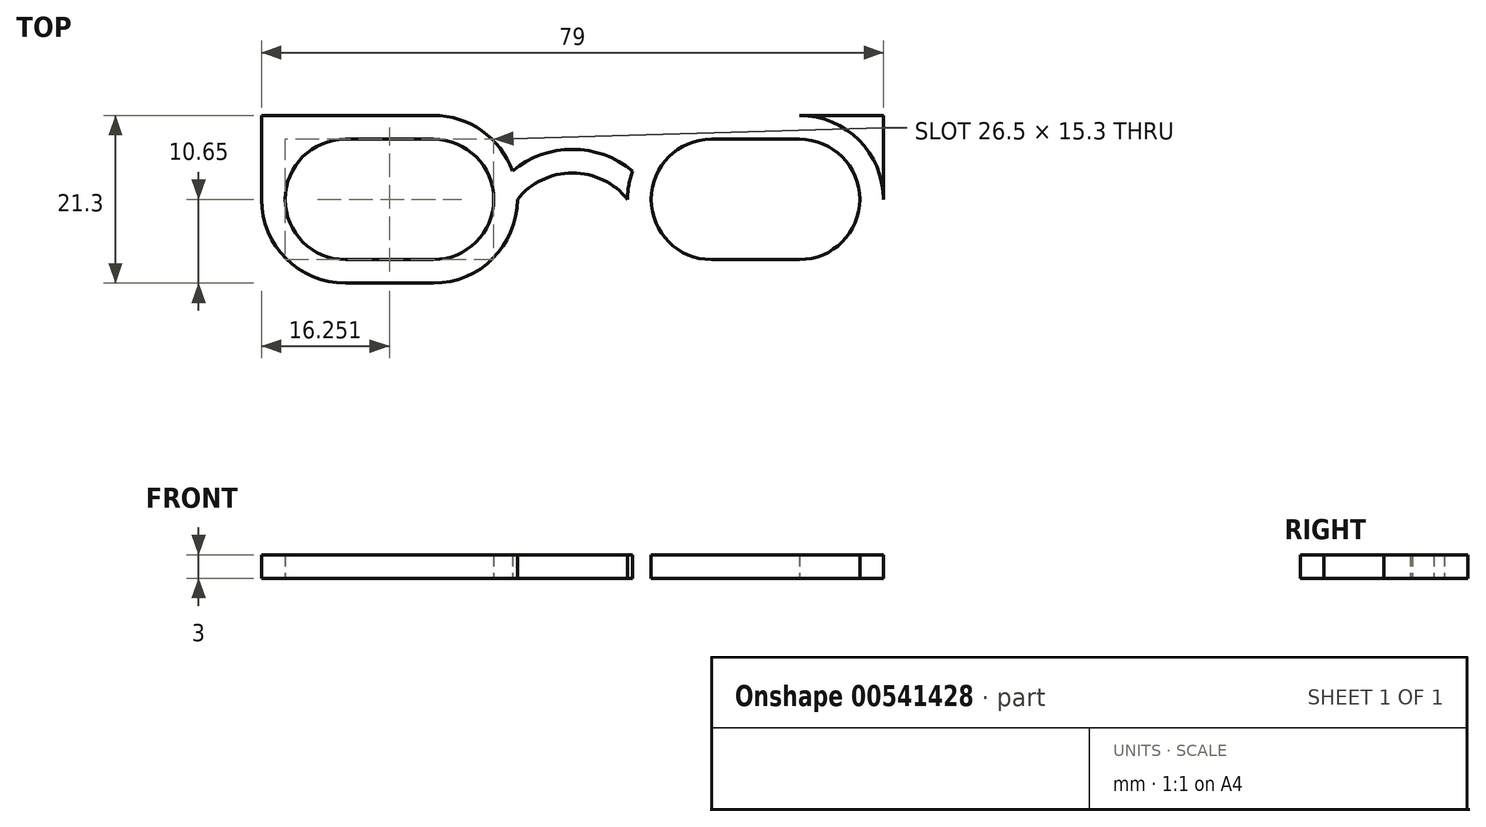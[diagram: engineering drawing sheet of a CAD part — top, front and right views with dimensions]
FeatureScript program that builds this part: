
annotation { "Feature Type Name" : "Feature", "Feature Type Description" : "" }
export const myFeature = defineFeature(function(context is Context, id is Id, definition is map)
    precondition{}
    {
        {
            var Q0;
            Q0=qCreatedBy(makeId("Top.planeOp"),FACE);
            var sketch = newSketch(context, id + "F0", { "sketchPlane" : qUnion([Q0])});
            skLineSegment(sketch, "E0", {"start": v(0, 24.47) * mm, "end": v(0, -25.63) * mm, "construction": true});
            skPoint(sketch, "E1", {"position": v(0, -41.55) * mm});
            skLineSegment(sketch, "E2", {"start": v(-35, -41.55) * mm, "end": v(35, -41.55) * mm, "construction": true});
            skPoint(sketch, "E3", {"position": v(-10, 0) * mm});
            skArc(sketch, "E4", {"start": v(-17.65, -7.65) * mm, "mid": v(-10, 0) * mm, "end": v(-17.65, 7.65) * mm});
            skLineSegment(sketch, "E5", {"start": v(-17.65, -7.65) * mm, "end": v(-28.85, -7.65) * mm});
            skLineSegment(sketch, "E6", {"start": v(-17.65, 7.65) * mm, "end": v(-28.85, 7.65) * mm});
            skArc(sketch, "E7", {"start": v(-28.85, 7.65) * mm, "mid": v(-36.5, 0) * mm, "end": v(-28.85, -7.65) * mm});
            skArc(sketch, "E8.MirrorCS", {"start": v(17.65, -7.65) * mm, "mid": v(10, 0) * mm, "end": v(17.65, 7.65) * mm});
            skLineSegment(sketch, "E9.MirrorCS", {"start": v(17.65, 7.65) * mm, "end": v(28.85, 7.65) * mm});
            skLineSegment(sketch, "E10.MirrorCS", {"start": v(17.65, -7.65) * mm, "end": v(28.85, -7.65) * mm});
            skArc(sketch, "E11.MirrorCS", {"start": v(28.85, 7.65) * mm, "mid": v(36.5, 0) * mm, "end": v(28.85, -7.65) * mm});
            skPoint(sketch, "E12", {"position": v(10, 0) * mm});
            skArc(sketch, "E13.0", {"start": v(-28.85, 10.65) * mm, "mid": v(-39.5, 0) * mm, "end": v(-28.85, -10.65) * mm});
            skLineSegment(sketch, "E13.1", {"start": v(-17.65, 10.65) * mm, "end": v(-28.85, 10.65) * mm});
            skArc(sketch, "E13.2", {"start": v(-17.65, -10.65) * mm, "mid": v(-7, 0) * mm, "end": v(-17.65, 10.65) * mm});
            skLineSegment(sketch, "E13.3", {"start": v(-17.65, -10.65) * mm, "end": v(-28.85, -10.65) * mm});
            skArc(sketch, "E14.MirrorCS", {"start": v(17.65, -10.65) * mm, "mid": v(7, 0) * mm, "end": v(17.65, 10.65) * mm});
            skLineSegment(sketch, "E15.MirrorCS", {"start": v(17.65, 10.65) * mm, "end": v(28.85, 10.65) * mm});
            skArc(sketch, "E16.MirrorCS", {"start": v(28.85, 10.65) * mm, "mid": v(39.5, 0) * mm, "end": v(28.85, -10.65) * mm});
            skLineSegment(sketch, "E17.MirrorCS", {"start": v(17.65, -10.65) * mm, "end": v(28.85, -10.65) * mm});
            skLineSegment(sketch, "E18", {"start": v(-39.5, 0) * mm, "end": v(-39.5, 10.65) * mm});
            skLineSegment(sketch, "E19", {"start": v(-28.85, 10.65) * mm, "end": v(-39.5, 10.65) * mm});
            skArc(sketch, "E20", {"start": v(7, 0) * mm, "mid": v(0, 3.35) * mm, "end": v(-7, 0) * mm});
            skArc(sketch, "E21.0", {"start": v(9.34, 1.88) * mm, "mid": v(0, 6.35) * mm, "end": v(-9.34, 1.88) * mm});
            skLineSegment(sketch, "E22.MirrorCS", {"start": v(28.85, 10.65) * mm, "end": v(39.5, 10.65) * mm});
            skLineSegment(sketch, "E23.MirrorCS", {"start": v(39.5, 0) * mm, "end": v(39.5, 10.65) * mm});
            skPoint(sketch, "E24.orphan", {"position": v(17.65, 7.65) * mm});
            skPoint(sketch, "E25.MirrorCS.end.orphan", {"position": v(17.65, -7.65) * mm});
            skPoint(sketch, "E26.orphan", {"position": v(28.85, -7.65) * mm});
            skPoint(sketch, "E27.MirrorCS.start.orphan", {"position": v(28.85, 7.65) * mm});
            skSolve(sketch);
        }
        {
            var Q0;
            {var subQ2=sQuery(id+"F0.wireOp",EDGE,"E18");Q0=makeQuery(id+"F0.imprint","IMPRINT",FACE,{"disambiguationData":[TD([[makeQuery(id+"F0.imprint","IMPRINT",EDGE,{"derivedFrom":subQ2}),-1.0]])]});}
            var Q1;
            Q1=makeQuery(id+"F0.imprint","IMPRINT",FACE,{"disambiguationData":[TD([[makeQuery(id+"F0.imprint","IMPRINT",EDGE,{"derivedFrom":sQuery(id+"F0.wireOp",EDGE,"E4")}),-1.0]])]});
            var Q2;
            {var subQ0=sQuery(id+"F0.wireOp",EDGE,"E20");Q2=makeQuery(id+"F0.imprint","IMPRINT",FACE,{"disambiguationData":[TD([[makeQuery(id+"F0.imprint","IMPRINT",EDGE,{"derivedFrom":subQ0}),-1.0]])]});}
            var Q3;
            Q3=makeQuery(id+"F0.imprint","IMPRINT",FACE,{"disambiguationData":[TD([[makeQuery(id+"F0.imprint","IMPRINT",EDGE,{"derivedFrom":sQuery(id+"F0.wireOp",EDGE,"E8.MirrorCS")}),1.0]])]});
            var Q4;
            {var subQ0=sQuery(id+"F0.wireOp",EDGE,"E22.MirrorCS");Q4=makeQuery(id+"F0.imprint","IMPRINT",FACE,{"disambiguationData":[TD([[makeQuery(id+"F0.imprint","IMPRINT",EDGE,{"derivedFrom":subQ0}),-1.0]])]});}
            extrude(context, id + "F1", {"entities" : qUnion([Q0, Q1, Q2, Q3, Q4]), "depth" : 3 * mm, "offsetDistance" : 25 * mm});
        }
    });
